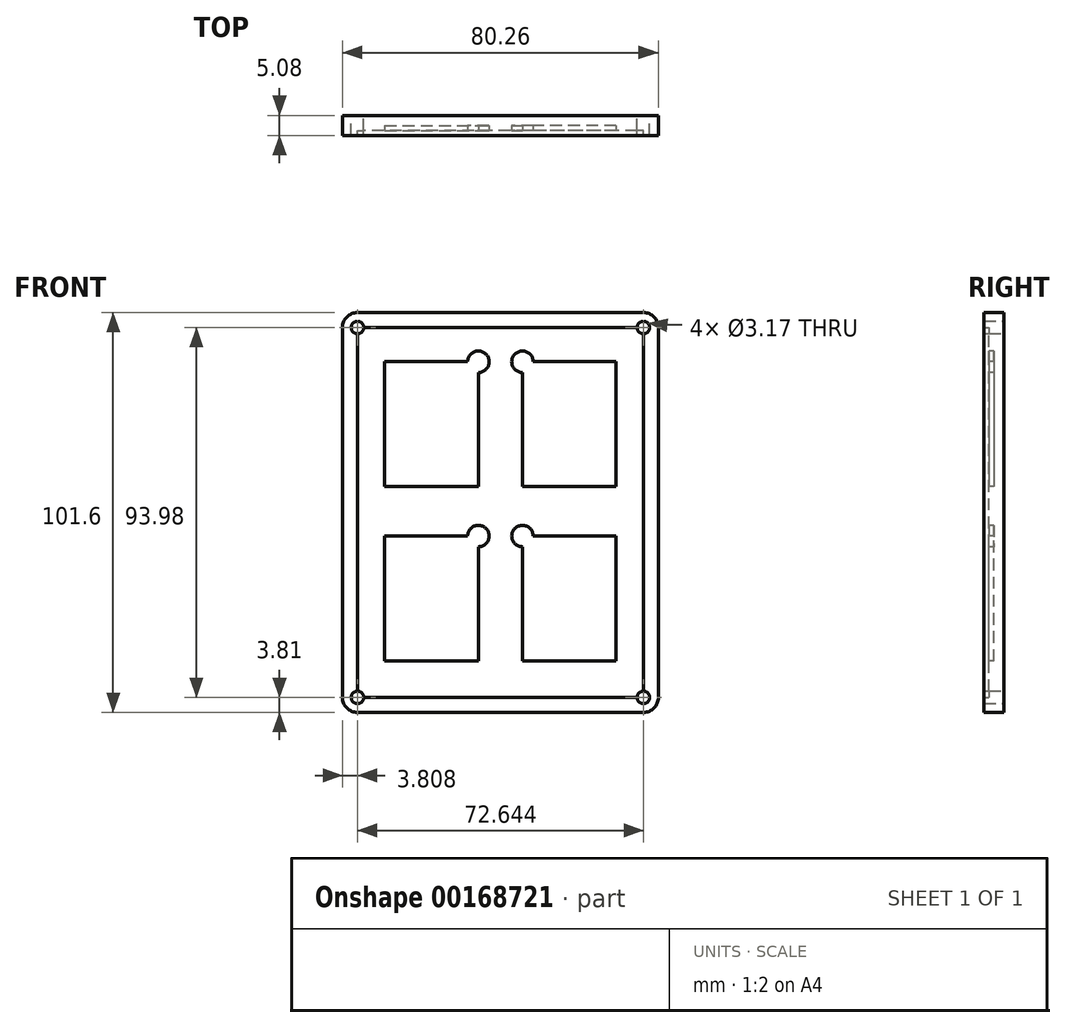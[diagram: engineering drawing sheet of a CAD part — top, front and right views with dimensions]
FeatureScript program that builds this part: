
annotation { "Feature Type Name" : "Feature", "Feature Type Description" : "" }
export const myFeature = defineFeature(function(context is Context, id is Id, definition is map)
    precondition{}
    {
        {
            var Q0;
            Q0=qCreatedBy(makeId("Front.planeOp"),FACE);
            var sketch = newSketch(context, id + "F0", { "sketchPlane" : qUnion([Q0])});
            skLineSegment(sketch, "E0.bottom", {"start": v(40.13, -50.8) * mm, "end": v(-40.13, -50.8) * mm});
            skLineSegment(sketch, "E0.top", {"start": v(40.13, 50.8) * mm, "end": v(-40.13, 50.8) * mm});
            skLineSegment(sketch, "E0.left", {"start": v(40.13, -50.8) * mm, "end": v(40.13, 50.8) * mm});
            skLineSegment(sketch, "E0.right", {"start": v(-40.13, -50.8) * mm, "end": v(-40.13, 50.8) * mm});
            skPoint(sketch, "E0.middle", {"position": v(0, 0) * mm});
            skSolve(sketch);
        }
        {
            var Q0;
            Q0 = qSketchRegion(id + "F0", true);
            extrude(context, id + "F1", {"entities" : qUnion([Q0]), "depth" : 5.08 * mm, "symmetric" : true});
        }
        {
            var Q0;
            Q0=makeQuery(id+"F1.opExtrude","SWEPT_EDGE",EDGE,{"disambiguationData":[OSD([sQuery(id+"F0.wireOp",EDGE,"E0.top"),sQuery(id+"F0.wireOp",EDGE,"E0.right")])]});
            var Q1;
            Q1=makeQuery(id+"F1.opExtrude","SWEPT_EDGE",EDGE,{"disambiguationData":[OSD([sQuery(id+"F0.wireOp",EDGE,"E0.top"),sQuery(id+"F0.wireOp",EDGE,"E0.left")])]});
            var Q2;
            Q2=makeQuery(id+"F1.opExtrude","SWEPT_EDGE",EDGE,{"disambiguationData":[OSD([sQuery(id+"F0.wireOp",EDGE,"E0.bottom"),sQuery(id+"F0.wireOp",EDGE,"E0.left")])]});
            var Q3;
            Q3=makeQuery(id+"F1.opExtrude","SWEPT_EDGE",EDGE,{"disambiguationData":[OSD([sQuery(id+"F0.wireOp",EDGE,"E0.bottom"),sQuery(id+"F0.wireOp",EDGE,"E0.right")])]});
            fillet(context, id + "F2", {"entities" : qUnion([Q0, Q1, Q2, Q3]), "radius" : 3.8 * mm, "tangentPropagation" : true, "allowEdgeOverflow" : false});
        }
        {
            var Q0;
            Q0=makeQuery(id+"F1.opExtrude","CAP_FACE",FACE,{"disambiguationData":[OSD([sQuery(id+"F0.wireOp",EDGE,"E0.bottom"),sQuery(id+"F0.wireOp",EDGE,"E0.top"),sQuery(id+"F0.wireOp",EDGE,"E0.left"),sQuery(id+"F0.wireOp",EDGE,"E0.right")])],"isStart":false});
            var sketch = newSketch(context, id + "F3", { "sketchPlane" : qUnion([Q0])});
            skLineSegment(sketch, "E1.bottom", {"start": v(36.32, -46.99) * mm, "end": v(-36.32, -46.99) * mm});
            skLineSegment(sketch, "E1.top", {"start": v(36.32, 46.99) * mm, "end": v(-36.32, 46.99) * mm});
            skLineSegment(sketch, "E1.left", {"start": v(36.32, -46.99) * mm, "end": v(36.32, 46.99) * mm});
            skLineSegment(sketch, "E1.right", {"start": v(-36.32, -46.99) * mm, "end": v(-36.32, 46.99) * mm});
            skPoint(sketch, "E1.middle", {"position": v(0, 0) * mm});
            skSolve(sketch);
        }
        {
            var Q0;
            Q0 = qSketchRegion(id + "F3", true);
            extrude(context, id + "F4", {"entities" : qUnion([Q0]), "operationType" : NewBodyOperationType.REMOVE, "oppositeDirection" : true, "depth" : 1.27 * mm});
        }
        {
            var Q0;
            Q0=makeQuery(id+"F4.boolean.opBoolean","COPY",FACE,{"derivedFrom":makeQuery(id+"F4.opExtrude","CAP_FACE",FACE,{"disambiguationData":[OSD([sQuery(id+"F3.wireOp",EDGE,"E1.bottom"),sQuery(id+"F3.wireOp",EDGE,"E1.top"),sQuery(id+"F3.wireOp",EDGE,"E1.left"),sQuery(id+"F3.wireOp",EDGE,"E1.right")])],"isStart":false})});
            var sketch = newSketch(context, id + "F5", { "sketchPlane" : qUnion([Q0])});
            skLineSegment(sketch, "E2.bottom", {"start": v(-29.41, 38.3) * mm, "end": v(-5.6, 38.3) * mm});
            skLineSegment(sketch, "E2.top", {"start": v(-29.41, 6.54) * mm, "end": v(-5.6, 6.54) * mm});
            skLineSegment(sketch, "E2.left", {"start": v(-29.41, 38.3) * mm, "end": v(-29.41, 6.54) * mm});
            skLineSegment(sketch, "E2.right", {"start": v(-5.6, 38.3) * mm, "end": v(-5.6, 6.54) * mm});
            skLineSegment(sketch, "E3.MirrorCS", {"start": v(29.41, 38.3) * mm, "end": v(5.6, 38.3) * mm});
            skLineSegment(sketch, "E4.MirrorCS", {"start": v(29.41, 38.3) * mm, "end": v(29.41, 6.54) * mm});
            skLineSegment(sketch, "E5.MirrorCS", {"start": v(29.41, 6.54) * mm, "end": v(5.6, 6.54) * mm});
            skLineSegment(sketch, "E6.MirrorCS", {"start": v(5.6, 38.3) * mm, "end": v(5.6, 6.54) * mm});
            skSolve(sketch);
        }
        {
            var Q0;
            Q0 = qSketchRegion(id + "F5", true);
            extrude(context, id + "F6", {"entities" : qUnion([Q0]), "operationType" : NewBodyOperationType.REMOVE, "oppositeDirection" : true, "depth" : 2.54 * mm, "symmetric" : true});
        }
        {
            var Q0;
            Q0=makeQuery(id+"F4.boolean.opBoolean","COPY",FACE,{"derivedFrom":makeQuery(id+"F4.opExtrude","CAP_FACE",FACE,{"disambiguationData":[OSD([sQuery(id+"F3.wireOp",EDGE,"E1.bottom"),sQuery(id+"F3.wireOp",EDGE,"E1.top"),sQuery(id+"F3.wireOp",EDGE,"E1.left"),sQuery(id+"F3.wireOp",EDGE,"E1.right")])],"isStart":false})});
            var sketch = newSketch(context, id + "F7", { "sketchPlane" : qUnion([Q0])});
            skLineSegment(sketch, "E7.bottom", {"start": v(-29.41, -37.74) * mm, "end": v(-5.6, -37.74) * mm});
            skLineSegment(sketch, "E7.top", {"start": v(-29.41, -5.99) * mm, "end": v(-5.6, -5.99) * mm});
            skLineSegment(sketch, "E7.left", {"start": v(-29.41, -37.74) * mm, "end": v(-29.41, -5.99) * mm});
            skLineSegment(sketch, "E7.right", {"start": v(-5.6, -37.74) * mm, "end": v(-5.6, -5.99) * mm});
            skLineSegment(sketch, "E8.MirrorCS", {"start": v(29.41, -5.99) * mm, "end": v(5.6, -5.99) * mm});
            skLineSegment(sketch, "E9.MirrorCS", {"start": v(29.41, -37.74) * mm, "end": v(29.41, -5.99) * mm});
            skLineSegment(sketch, "E10.MirrorCS", {"start": v(29.41, -37.74) * mm, "end": v(5.6, -37.74) * mm});
            skLineSegment(sketch, "E11.MirrorCS", {"start": v(5.6, -37.74) * mm, "end": v(5.6, -5.99) * mm});
            skSolve(sketch);
        }
        {
            var Q0;
            Q0 = qSketchRegion(id + "F7", true);
            extrude(context, id + "F8", {"entities" : qUnion([Q0]), "operationType" : NewBodyOperationType.REMOVE, "oppositeDirection" : true, "depth" : 2.54 * mm, "symmetric" : true});
        }
        {
            var Q0;
            Q0=makeQuery(id+"F4.boolean.opBoolean","COPY",FACE,{"derivedFrom":makeQuery(id+"F4.opExtrude","CAP_FACE",FACE,{"disambiguationData":[OSD([sQuery(id+"F3.wireOp",EDGE,"E1.bottom"),sQuery(id+"F3.wireOp",EDGE,"E1.top"),sQuery(id+"F3.wireOp",EDGE,"E1.left"),sQuery(id+"F3.wireOp",EDGE,"E1.right")])],"isStart":false})});
            var sketch = newSketch(context, id + "F9", { "sketchPlane" : qUnion([Q0])});
            skCircle(sketch, "E12", {"center": v(-5.6, 38.3) * mm, "radius": 2.73 * mm});
            skCircle(sketch, "E13", {"center": v(-5.6, -5.99) * mm, "radius": 2.73 * mm});
            skCircle(sketch, "E14.MirrorC", {"center": v(5.6, 38.3) * mm, "radius": 2.73 * mm});
            skCircle(sketch, "E15.MirrorC", {"center": v(5.6, -5.99) * mm, "radius": 2.73 * mm});
            skSolve(sketch);
        }
        {
            var Q0;
            Q0 = qSketchRegion(id + "F9", true);
            extrude(context, id + "F10", {"entities" : qUnion([Q0]), "operationType" : NewBodyOperationType.REMOVE, "oppositeDirection" : true, "depth" : 1.27 * mm});
        }
        {
            var Q0;
            Q0=makeQuery(id+"F1.opExtrude","CAP_FACE",FACE,{"disambiguationData":[OSD([sQuery(id+"F0.wireOp",EDGE,"E0.bottom"),sQuery(id+"F0.wireOp",EDGE,"E0.top"),sQuery(id+"F0.wireOp",EDGE,"E0.left"),sQuery(id+"F0.wireOp",EDGE,"E0.right")])],"isStart":true});
            var sketch = newSketch(context, id + "F11", { "sketchPlane" : qUnion([Q0])});
            skPoint(sketch, "E16", {"position": v(-36.32, 47) * mm});
            skPoint(sketch, "E17", {"position": v(36.32, 46.99) * mm});
            skPoint(sketch, "E18", {"position": v(36.32, -47) * mm});
            skPoint(sketch, "E19", {"position": v(-36.32, -46.99) * mm});
            skSolve(sketch);
        }
        {
            var Q0;
            Q0=sQuery(id+"F11.wireOp",VERTEX,"E16");
            var Q1;
            Q1=sQuery(id+"F11.wireOp",VERTEX,"E17");
            var Q2;
            Q2=sQuery(id+"F11.wireOp",VERTEX,"E18");
            var Q3;
            Q3=sQuery(id+"F11.wireOp",VERTEX,"E19");
            var Q4;
            Q4=makeQuery(id+"F1.opExtrude","SWEPT_BODY",BODY,{"disambiguationData":[OSD([sQuery(id+"F0.wireOp",EDGE,"E0.bottom"),sQuery(id+"F0.wireOp",EDGE,"E0.top"),sQuery(id+"F0.wireOp",EDGE,"E0.left"),sQuery(id+"F0.wireOp",EDGE,"E0.right")])]});
            hole(context, id + "F12", {"style" : HoleStyle.SIMPLE, "endStyle" : HoleEndStyle.BLIND, "holeDiameter" : 3.17 * mm, "holeDepth" : 9.52 * mm, "locations" : qUnion([Q0, Q1, Q2, Q3]), "scope" : qUnion([Q4])});
        }
    });
